# Revit family: 2015_Ventana_Alueuropa_Q77_1-Hoja_Practicable-Oscilobatiente
name_source: partatom
category: Windows
revit_build: Autodesk Revit 2015 (Build: 20140223_1515(x64)
units: mm (PartAtom-declared; Revit-internal decimal feet)

## types (2) — shared parameters
Acristalamiento = Cristal - Vidrio claro templado
Altura Máxima = 5000 mm  [stored 16.4042 ft]
Altura Real = 1000 mm  [stored 3.28084 ft]
Altura de antepecho por defecto = 800 mm  [stored 2.62467 ft]
Anchura Máxima = 5000 mm  [stored 16.4042 ft]
Anchura Real = 600 mm  [stored 1.9685 ft]
Area = 600000 mm²
Autor = Bimetica Parametric Design Services, S.L.
Bimetica = http://www.bimetica.com
CerramientoExterior = Yes
ConfiguracionPoliamidas = 273800 - 493700 - 493800
ControlHumos = No
CosteEnergeticoMj = 0 J
Desfase Acristalamiento = 13 mm
Detalle Perfileria = Yes
FactorSolarModificado = 3000000
FechaEmisionElementoBIM = 23/08/2016
FechaVencimientoElementoBIM = 23/08/2017
FraccionAreaAcristalamiento = 0.00%
GrosorAcristalamiento = 30 mm  [stored 0.0984252 ft]
GrosorMarco = 77 mm  [stored 0.252625 ft]
Height = 1000 mm  [stored 3.28084 ft]
InformacionTecnica = http://www.alueuropa.com
Manija = Yes
Manufacturer = Alueuropa S.A.
Marco = Aluminio
MasterformatCodigo = 08 51 13
MasterformatTitulo = Aluminium Windows
Motorizada = No
OmniclassCodigo = 23.30.20.17.21.21
OmniclassTitulo = Casment Window
Perimetro = 3200
Poliamida = Poliamida, Technoform Bautec, PA66 GF 25
Practicable = Yes
Proyección Apertura = Yes
ReferenciaContacto = Alueuropa S.A.
RepisaExterior = Yes
RepisaInterior = Yes
Rough Height = 605 mm
Rough Width = 1005 mm  [stored 3.29724 ft]
SalidaEmergencia = No
TelefonoContacto = +34 91 8955800
UNSPSCCodigo = 30171600
UNSPSCTitulo = Windows
URL = http://www.alueuropa.com
URL Poliamida = http://www.technoform.es
URL Poliamida - Catálogo = http://www.technoform.com
URLProducto = http://www.alueuropa.com
Uniclass2.0Codigo = 25-30
Uniclass2.0Titulo = Door and window systems
VersionElementoBIM = 1.0
Wall Closure = By host
Width = 600 mm  [stored 1.9685 ft]
Y𝑔 = 0.11
𝐴𝑓 = 245616
𝐴𝑔 = 354384
𝑈𝑓 = 3.629
𝑈𝑔 = 1.9
𝑈𝑤 = 3.068317
𝑙𝑔 = 2512
zero-valued in all types: AcidificacionAtmosferica, AcidificacionAtmosfericaPorUnidad, AguaConsumida, AguaConsumidaPorUnidad, CambioClimatico, CambioClimaticoPorUnidad, CosteEnergeticoKwh, CosteMantenimiento, DestruccionCapaOzonoEstratosferica, DestruccionCapaOzonoEstratosfericaPorUnidad, EmisionCO2, EnergiaNoRenovableConsumida, EnergiaNoRenovableConsumidaPorUnidad, EnergiaPrimariaTotalConsumida, EnergiaPrimariaTotalConsumidaPorUnidad, EnergiaRenovableConsumida, EnergiaRenovableConsumidaPorUnidad, Eutrofizacion, EutrofizacionPorUnidad, FactorSombra, FaltaDeRecursos, FaltaDeRecursosPorUnidad, FormacionFotoquimicaOzono, FormacionFotoquimicaOzonoPorUnidad, MasaSuperficialKgm2, MateriaPrima, ResiduoInerte, ResiduoInertePorUnidad, ResiduoRadioactivo, ResiduoRadioactivoPorUnidad, ResiduosNoPeligrosos, ResiduosNoPeligrososPorUnidad, ResiduosPeligrosos, ResiduosPeligrososPorUnidad, TransmitanciaTermica

## per-type parameters (varying)
| type | Description | Model | Operation | Oscilobatiente | Type Comments |
| 600x1000 mm Practicable | Ventana Practicable | Q77 Practicable | Practicable | No | Sistema de Ventana con Rotura de Puente Térmico Q77 Practicable. |
| 600x1000 mm Oscilobatiente | Ventana Oscilobatiente | Q77 Oscilobatiente | Oscilobatiente | Yes | Sistema de Ventana con Rotura de Puente Térmico Q77 Oscilobatiente. |

note: [stored X ft] marks values corroborated as IEEE doubles in the binary element streams (Revit-internal decimal feet)
